# Revit family: BCS (C) Base unit - 2957UK.RFA
name_source: partatom
category: Mechanical Equipment
revit_build: Autodesk Revit MEP 2015 (Build: 20150303_1515(x64)
units: mm (PartAtom-declared; Revit-internal decimal feet)

## types (1)
- HT1760/1761 BCS (Compact 100/140) 75G4
    6 Monthly Maintenance (or SFG20 Codes) = Required (uk) 6 months service (including filter change)
    Backflow Prevention Valve = No
    Base Unit Finish = White Enamel
    Button Interface = NO  (LCD Touch Screen supplied)
    Cable Length and size (If Fitted) = 3.0m nominal
    Internal Filter (if fitted) = Supplied
    Life Cycle Analysis = Not Known
    Location of Manufacturer = Australia
    Mains Pressure Limiting Valve = Supplied
    Mains Water Connection = I/2" BSP
    Mains Water Pressure _ Maximum = 0.7 MPa (7 bar)
    Mains Water Pressure _ Minimum = 0.25 MPa (2.5 bar)
    Manufacturer = Zip Industries(UK) Ltd
    Max. Stored Water Temperature = 98°C
    Model = BCS PRT No 2957UK
    Net Weight = 30kg
    Nominal Flow Rate (Boiling) = 1.2L/min
    Overall Height = 333mm
    Overall Length/Depth = 461mm
    Overall Width = 338mm
    Power Rating = 2.13kW
    Power Supply (Voltage) = 220-240V AC 13A
    Product Range = HydroTap
    Programmable Function Parameters = Supplied
    Programmable Safety Features = YES
    Shape = Rectangular
    Standby Power Loss (idle mode) = Not Known
    Supply Phase = single phase
    Tank Construction Material = Stainless Steel
    Type = Command Centre
    Type Comments = Boiling Water Heater (Potable)
    URL = www.zipindustries.co.uk
    Unit Access Clearance Bottom = 0mm
    Unit Access Clearance Front = 40mm
    Unit Access Clearance Left = 50mm
    Unit Access Clearance Rear = 0mm
    Unit Access Clearance Top = 202mm
    Unit Access Clearance right = 50mm
    WRAS Approved = Yes
    Wireless (WIFI) = TBC

## geometry (parser evidence)
native form markers: Sweep x2
no freeform markers — native parametric forms only
